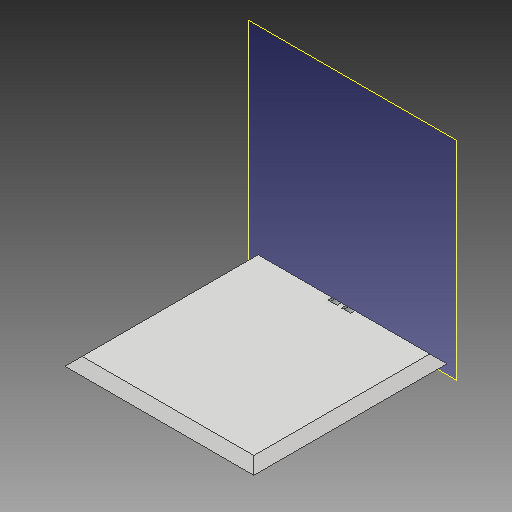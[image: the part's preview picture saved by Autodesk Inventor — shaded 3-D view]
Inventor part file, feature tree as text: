
AUTODESK INVENTOR PART (.ipt)
format: ipt  version: 2018 (Build 220112000, 112)  size: 114,176 bytes
history: native  units: mm
features: other x7, sketch x3, extrude x2, plane x1
ambient origin geometry x8: Origin, YZ Plane, XZ Plane, XY Plane, X Axis, Y Axis, Z Axis, Center Point
bodies: Volumenkörper1 (feature_tree)
feature tree (13):
  other  "Wand1.ipt"
  plane  "Arbeitsebene5"
  extrude  "Extrusion5"  Depth=10.0mm
  extrude  "Extrusion6"  Depth=21.0mm
  other  "Volumenkörper1::Wand1.ipt"
  other  "Bezeichnung1"
  sketch  "Skizze1"  dims[d0=10.0mm d33=5.0mm]
  other  "Arbeitspunkt6"
  sketch  "Skizze8"  dims[d34=5.0mm d35=21.0mm]
  sketch  "Skizze9"  dims[d36=174.5mm d37=30.0mm d38=0.0mm d39=5.0mm d40=5.0mm d41=21.0mm d42=30.0mm d43=0.0mm]
  parser-record x1  (decoder bookkeeping rows leaked as tree rows — omitted from the tree; the rows remain in map.json)
  other  "SmartCube_Quadratisch.iam"
  other  "Wand2_MIR:1"
note: 1 file-system path scrubbed to <path> (originals preserved in map.json)
